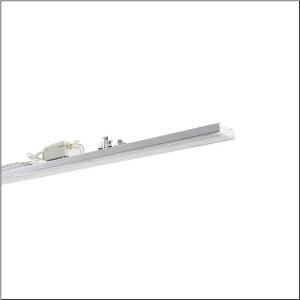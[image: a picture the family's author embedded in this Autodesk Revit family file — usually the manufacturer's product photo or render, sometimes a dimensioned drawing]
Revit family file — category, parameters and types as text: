
# Revit family: licross_r__21_recessed_mo_52te11dv4fxg_dcfe
name_source: partatom
category: Lighting Fixtures
units: mm (PartAtom-declared; Revit-internal decimal feet)

## family parameters
Cut with Voids When Loaded = No
Host = Face
Light Source = No
Part Type = Normal
Room Calculation Point = No
Round Connector Dimension = Use Diameter
Shared = No

## types (1)
- --- (1 x LED, 15180 lm, 85.3 W, 4000K)
    Apparent Load = 85 VA
    CIE Flux Codes = 89 96 99 100 100
    Color Rendering = 80
    Color Temperature = 4000K
    Default Elevation = 1800 mm
    Description = Licross® 21 Recessed MO, luminaire insert, of sheet steel, galvanised, coil coated, white, length: 2.250mm, width: 66mm, height: 67mm, LED rated luminous flux: 15.180lm, light colour: 840, control gear: DALI 2, with plug, 5-pole, with phase selection, mains connection: 220..240V, AC, 50/60Hz, rated input power: 85W, halogen-free wiring, primary light control with lens, of plastic, primary optical cover: cover, of PMMA, light emission: direct distribution, primary light characteristic: symmetric, protection rating (complete): IP54, insulation class (complete): insulation class I (protective earthing), certification: CE, ENEC, VDE, UKCA, protection symbol: D if used in an environment with non-conductive dust loads with corresponding accessories, impact resistance: IK06, permissible ambient temperature for indoor applications: -25..+35°C, corresponds to IFS (International Featured Standards) requirements for safety and quality in the food industry, reducing of maximum allowable ambient temperature of 5°C with ceiling mounting, LABS conformity tested according to VDMA 24364:2018-05, packaging unit: 1 piece
    Height = 58 mm
    Lamp = 1 x LED
    Lamp Light Flux = 15180 lm
    Lamp Power = 85.3 W
    Lamp count = 1
    Length = 2250 mm
    Luminous efficacy = 178 lm/W
    Manufacturer = Siteco
    ModVariant = No
    Model = 52TE11DV4FXG
    Mounting Place = Ceiling
    Mounting Type = Pendant
    Number of Poles = 1
    OnlyDefault = Yes
    Power Factor = 1
    Product Name = Licross® 21 Recessed MO
    Product group = luminaire insert
    ProductGroupID = 901
    Protection Class = Protection class I
    Protection Degree = IP 54
    RLX_Detail_Level = 1
    RLX_Emergency_Light_Flux = 0 lm
    RLX_Emergency_Type = 0
    RLX_Emergency_Type_DB = No
    RlxData = <blob elided: 29521 chars, md5=c7a60694>
    Socket = socket
    Standby Power = 0 W
    System Light Flux = 15180 lm
    System Power = 85 W
    Type Comments = factory setting: luminous flux: 100 % | dim-lin: 254 | 390 mA
    Type Image = l_1296930.jpg
    URL = http://relux.com
    VarID = @adj_058661
    Voltage = 0 V
    Weight = 0.00 kg
    Width = 66 mm

## geometry (parser evidence)
native form markers: Blend x4, Sweep x8
no freeform markers — native parametric forms only
